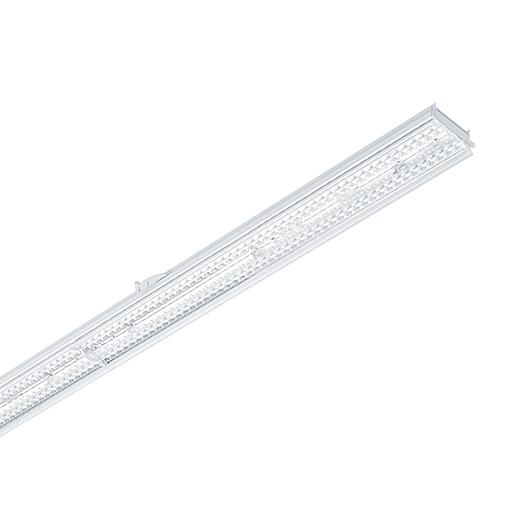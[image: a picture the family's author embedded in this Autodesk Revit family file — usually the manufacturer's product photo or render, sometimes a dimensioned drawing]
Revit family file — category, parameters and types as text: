
# Revit family: Zumtobel TECTON 2 Lighting Trunking System
name_source: partatom
category: Electrical Fixtures
units: mm (PartAtom-declared; Revit-internal decimal feet)

## family parameters
Cut with Voids When Loaded = Yes
Host = Face
Maintain Annotation Orientation = No
Part Type = Normal
Room Calculation Point = Yes
Round Connector Dimension = Use Diameter
Shared = No

## types (2) — shared parameters
A = 10000 mm  [stored 32.8084 ft]
ADDITIONAL INFORMATION - Luminaire Type Instructions = To use additional luminaires within the system, download the required models from the website and insert them into the project.
By default, the TECTON 2 System family includes only a few types of TECTON 2 Wide Beam continuous-row luminaires. 
To use other products from the TECTON 2 portfolio, locate the desired luminaires on the website, load them into the project, and set the Luminaire Type parameter to select the appropriate model.


After selecting the model, adjust the Luminaire Length parameter to ensure the cover strips are calculated correctly. 
Use the default lengths for continuous luminaires (1 m, 1.5 m, 2 m, 2.5 m), or, for custom lengths, use the Luminaire Length Other parameter and specify the exact dimension.


Secondary luminaires and elements such as PANOS 3, RESCLITE PRO, emergency lighting units, sensors, and similar components should be attached to the TECTON track as individual lighting fixtures, rather than as part of the TECTON System family.

* Download and insert luminaires
   - Access the required luminaire models from the website.
   - Insert them into the project.

* TECTON 2 System family default
   - Contains only a few types of TECTON 2 Wide Beam continuous-row luminaires.
   - For other TECTON 2 products, download the desired luminaires and load them into the project.

* Set Luminaire Type
   - Select the appropriate model using the Luminaire Type parameter.

* Set Luminaire Length
   - Adjust the Luminaire Length parameter to ensure cover strips are calculated correctly.
   - 

Use default lengths for continuous luminaires: 1 m, 1.5 m, 2 m, 2.5 m.


   - For custom lengths, use Luminaire Length Other and specify the exact dimension.

* Secondary luminaires and elements
   - 

PANOS 3, RESCLITE PRO, emergency lighting units, sensors, etc.
   - 

Attach these to the TECTON track as individual lighting fixtures.
   - 

Do not include them as part of the TECTON System family.
Caddy Clip = No
Ceiling Fixing Element = No
Chain Galvanised = No
Chain Non-rusting = No
Chain suspension with S hook = No
Chain suspension with carabiner = No
Cord Suspension = Yes
Count Luminaires = 6
Count Luminaires Final = 3
Count Luminaires Max = 6
Count Rails = 4
Cover Strip Design Flat = Yes
Cover Strip Design High = No
Cover Strip Lengt 1.5m = No
Cover Strip Lengt 2.5m = No
Cover Strip Lengt 2m = Yes
Cover Strips = 5500 mm  [stored 18.0446 ft]
D = 2000 mm  [stored 6.56168 ft]
DEFINE THE LENGTH OF THE LIGHTING TRUNKING SYSTEM = DEFINE THE LENGTH OF THE LIGHTING TRUNKING SYSTEM
Description = Lighting Trunking Systems
E = 2000 mm  [stored 6.56168 ft]
Electrical Output = No
Electrical Wiring For Feed-in = No
Electrical Wiring For Feed-out = No
Fixing Elements Offset From End = 300 mm  [stored 0.984252 ft]
Fixing Elements Offset From Start = 300 mm  [stored 0.984252 ft]
Fixing Elements Spacing = 1500 mm  [stored 4.92126 ft]
Lighting Trunking System Length = 10000 mm  [stored 32.8084 ft]
Lighting Trunking System With Cover Strips = Yes
Lighting Trunking System With Luminaires = Yes
Luminaire Length 1.5m = Yes
Luminaire Length 1m = No
Luminaire Length 2.5m = No
Luminaire Length 2m = No
Luminaire Length Other = 1000 mm  [stored 3.28084 ft]
Luminaires Number = 3
M = 2000 mm  [stored 6.56168 ft]
Manufacturer = Zumtobel Lighting
Mounting Rail 1.5m = No
Mounting Rail 2.5m = No
Mounting Rail 2m = Yes
Mounting Rail 3.5m = No
Mounting Rail 3m = No
Mounting Rail 4.5m = No
Mounting Rail 4m = No
Mounting Rail Feed 1.5m = No
Mounting Rail Feed 1m = No
Mounting Rail Feed 2.5m = No
Mounting Rail Feed 2m = Yes
N = 500 mm  [stored 1.64042 ft]
No Mounting Rail = No
P = 10000 mm  [stored 32.8084 ft]
Q = 10000 mm  [stored 32.8084 ft]
SELECT COVER OPTIONS = SELECT COVER OPTIONS
SELECT FIXING ELEMENT TYPE = SELECT FIXING ELEMENT TYPE
SELECT FIXING ELEMENTS POSITIONS = SELECT FIXING ELEMENTS POSITIONS
SELECT LIGHTING TRUNKING SYSTEM COLOR = SELECT LIGHTING TRUNKING SYSTEM COLOR
SELECT LUMINAIRES OPTIONS = SELECT LUMINAIRES OPTIONS
SELECT MOUNTING RAIL COMPONENTS = SELECT MOUNTING RAIL COMPONENTS
SELECT MOUNTING RAIL FEED TYPE = SELECT MOUNTING RAIL FEED TYPE
SELECT MOUNTING RAIL TYPE = SELECT MOUNTING RAIL TYPE
Spacing Module End = No
Spacing Module Start = No
Strain Relief = No
Trunking Length = 10000 mm  [stored 32.8084 ft]
Type Trunking Systems Black = Zumtobel-Parts-TECTON 2-Assembled : Black
Type Trunking Systems White = Zumtobel-Parts-TECTON 2-Assembled : White
URL = https://www.zumtobel.com II
Visibility Cover Strip High = No
Visibility Luminaires = Yes
Visibility Rail End = No
Visibility Rail End Second = No
ZA = 10000 mm  [stored 32.8084 ft]
ZF = 750 mm  [stored 2.46063 ft]
ZG = 750 mm  [stored 2.46063 ft]
ZL = 1500 mm  [stored 4.92126 ft]
zero-valued in all types: Default Elevation, F, G, Luminaire Offset From End, Luminaire Offset From Start, O, ZD, ZE

## per-type parameters (varying)
| type | Export Type to IFC As | Luminaire Type | Trunking System Black | Trunking System White | Type IFC Predefined Type | Type Trunking Systems |
| White 10000 suspended |  | Zumtobel TECTON 2 Wide Beam continuous row luminaire : TEC2 5k5-840 L15 WB LDE WH | No | Yes |  | Zumtobel-Parts-TECTON 2-Assembled : White |
| Black 10000 suspended | IfcLightFixtureType | Zumtobel TECTON 2 Wide Beam continuous row luminaire : TEC2 5k5-840 L15 WB LDE BK | Yes | No | NOTDEFINED | Zumtobel-Parts-TECTON 2-Assembled : Black |

note: [stored X ft] marks values corroborated as IEEE doubles in the binary element streams (Revit-internal decimal feet)

## geometry (parser evidence)
native form markers: Sweep x30
no freeform markers — native parametric forms only
